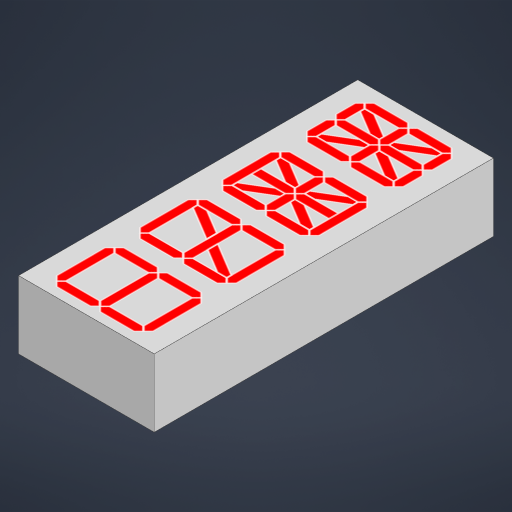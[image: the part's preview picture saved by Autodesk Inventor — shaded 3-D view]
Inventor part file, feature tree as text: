
AUTODESK INVENTOR PART (.ipt)
format: ipt  version: 2024.2 (Build 282272000, 272)  size: 193,536 bytes
history: native  units: mm
features: other x2, sketch x2, extrude x1
ambient origin geometry x8: Origin, YZ Plane, XZ Plane, XY Plane, X Axis, Y Axis, Z Axis, Center Point
bodies: Solid1 (feature_tree)
feature tree (5):
  extrude  "Extrusion1"  Depth=40.0mm
  other  "Decal1"
  sketch  "Sketch1"  dims[d0=16.0mm d1=40.0mm]
  sketch  "Sketch2"  dims[d2=8.0mm d3=0.0mm]
  other  "Image1"
